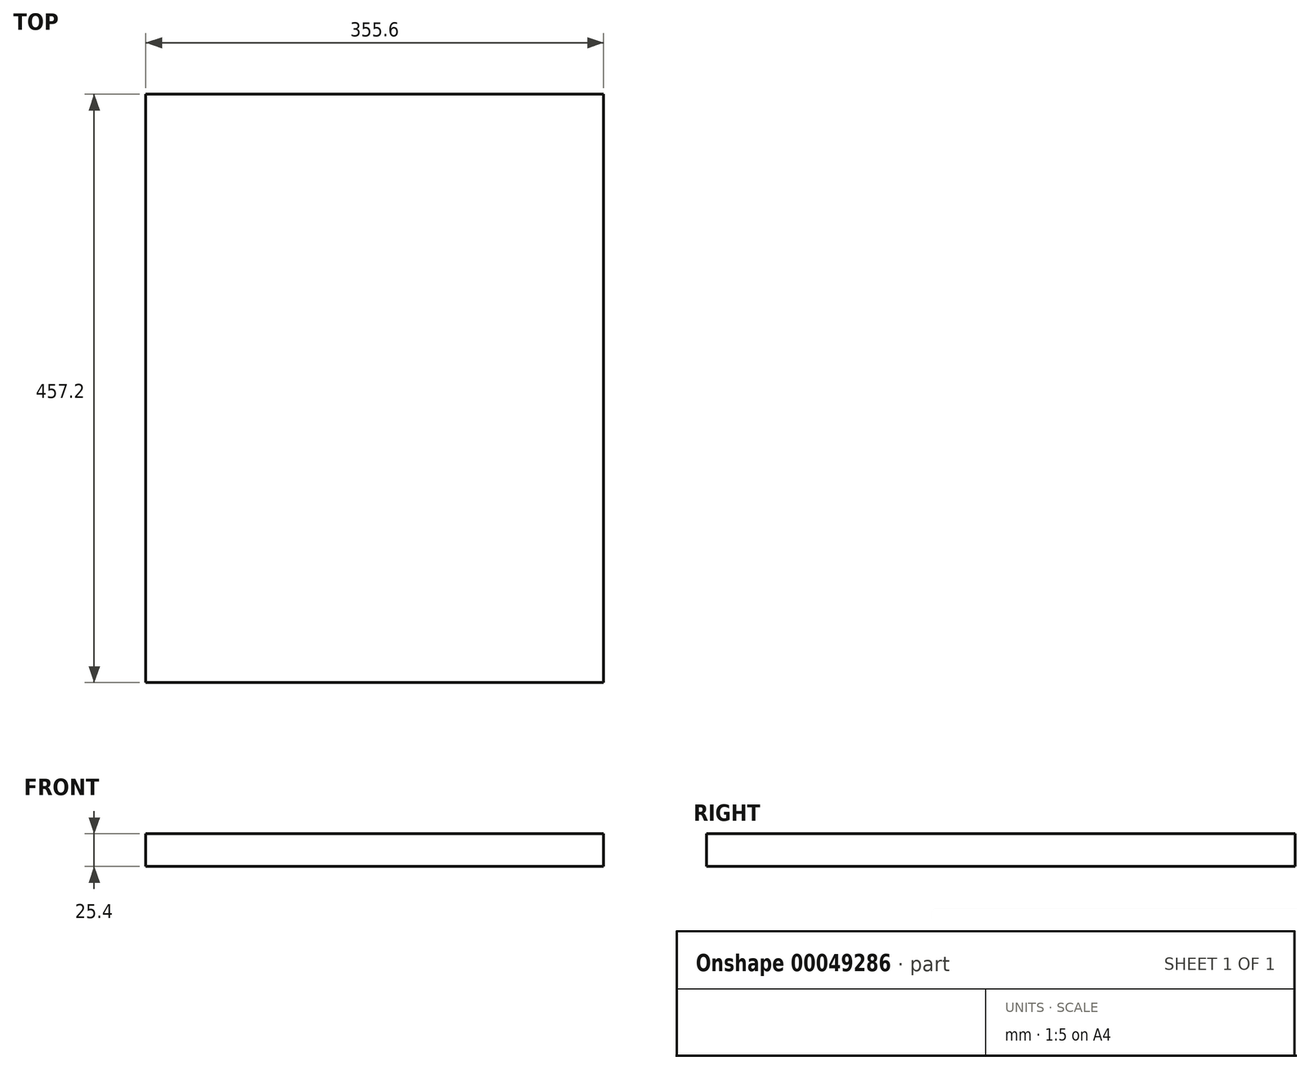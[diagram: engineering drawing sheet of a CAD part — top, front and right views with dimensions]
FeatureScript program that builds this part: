
annotation { "Feature Type Name" : "Feature", "Feature Type Description" : "" }
export const myFeature = defineFeature(function(context is Context, id is Id, definition is map)
    precondition{}
    {
        {
            var Q0;
            Q0=qCreatedBy(makeId("Top.planeOp"),FACE);
            var sketch = newSketch(context, id + "F0", { "sketchPlane" : qUnion([Q0])});
            skLineSegment(sketch, "E0.rect.bottom", {"start": v(153.27, -228.6) * mm, "end": v(-202.33, -228.6) * mm});
            skLineSegment(sketch, "E0.rect.top", {"start": v(153.27, 228.6) * mm, "end": v(-202.33, 228.6) * mm});
            skLineSegment(sketch, "E0.rect.left", {"start": v(153.27, -228.6) * mm, "end": v(153.27, 228.6) * mm});
            skLineSegment(sketch, "E0.rect.right", {"start": v(-202.33, -228.6) * mm, "end": v(-202.33, 228.6) * mm});
            skPoint(sketch, "E0.rect.middle", {"position": v(-24.53, 0) * mm});
            skSolve(sketch);
        }
        {
            var Q0;
            Q0 = qSketchRegion(id + "F0", true);
            extrude(context, id + "F1", {"entities" : qUnion([Q0]), "depth" : 25.4 * mm});
        }
    });
